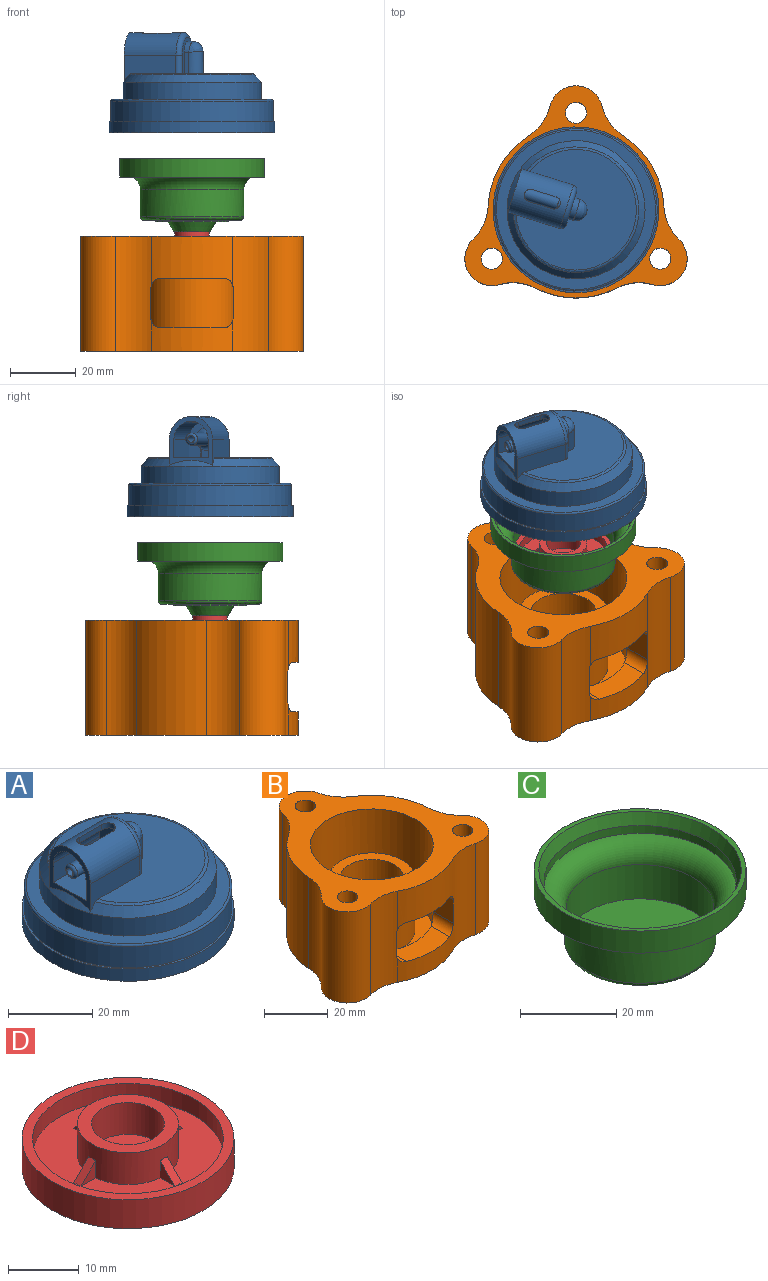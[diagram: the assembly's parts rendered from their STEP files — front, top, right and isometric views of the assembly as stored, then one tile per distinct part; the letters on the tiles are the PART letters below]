
ASSEMBLY  parts=4 mates=3
PART A: 80 faces, bbox 53.4x53.4x31 mm
  f0: plane 11x10.84mm, normal (-1,0,0), area 63mm2, adj f2,f65,f66,f67,f74,f75,f77
  f1: cylinder r=6.87mm len=16.5mm, axis (-1,0,0), area 315.8mm2, adj f9,f10,f55,f61,f70,f71,f72,f73
  f2: cylinder r=5.42mm len=15.2mm, axis (-1,0,0), area 218.2mm2, adj f0,f55,f65,f67,f70,f71,f72,f73
  f3: plane 2.2x2.2mm, normal (-1,0,0), area 0.7mm2, adj f62,f69
  f4: cone r=18.77mm half-angle=40deg, axis (0,0,-1), area 350.9mm2, adj f9,f10,f12,f27,f55
  f5: plane 6.43x1.45mm, normal (0,-1,0), area 9.3mm2, adj f6,f7,f11,f56
  f6: plane 11x10.74mm, normal (1,0,0), area 44.9mm2, adj f5,f8,f11,f56,f59,f60,f61
  f7: cylinder r=3.35mm len=6.8mm, axis (0,0,-1), area 70.2mm2, adj f5,f8,f11,f56,f57,f58
  f8: plane 6.45x1.45mm, normal (0,1,0), area 9.4mm2, adj f6,f7,f11,f56
  f9: plane 16.54x7.88mm, normal (0,-1,0), area 95.1mm2, adj f1,f4,f11,f12,f55,f60
  f10: plane 16.54x7.88mm, normal (0,1,0), area 95.1mm2, adj f1,f4,f11,f12,f55,f59
  f11: plane 36.6x35.27mm, normal (0,0,1), area 800.4mm2, adj f5,f6,f7,f8,f9,f10,f12,f59
  f12: torus R=18.3mm, axis (0,0,-1), area 90.3mm2, adj f4,f9,f10,f11
  f13: plane 36.6x36.6mm, normal (0,0,-1), area 1003.5mm2, adj f14,f29,f30,f31,f32,f35,f36,f37
  f14: cylinder r=18.3mm len=36.6mm, axis (0,0,-1), area 1494.8mm2, adj f13,f53
  f15: plane 38.5x38.5mm, normal (0,0,-1), area 6mm2, adj f53,f54
  f16: cylinder r=20.15mm len=40.3mm, axis (0,0,-1), area 312.7mm2, adj f17,f54
  f17: plane 43.8x43.8mm, normal (0,0,-1), area 231.2mm2, adj f16,f18
  f18: cylinder r=21.9mm len=43.8mm, axis (0,0,-1), area 371.5mm2, adj f17,f19
  f19: plane 47.3x47.3mm, normal (0,0,-1), area 250.4mm2, adj f18,f20
  f20: cylinder r=23.65mm len=47.3mm, axis (0,0,-1), area 662.7mm2, adj f19,f21
  f21: cone r=24.15mm half-angle=8deg, axis (0,0,-1), area 536.9mm2, adj f20,f22
  f22: plane 50.3x50.3mm, normal (0,0,-1), area 154.9mm2, adj f21,f23
  f23: cylinder r=25.15mm len=50.3mm, axis (0,0,-1), area 559.4mm2, adj f22,f24
  f24: plane 50.3x50.3mm, normal (0,0,1), area 78.2mm2, adj f23,f25
  f25: cylinder r=24.65mm len=49.3mm, axis (0,0,-1), area 944.8mm2, adj f24,f28
  f26: plane 48.3x48.3mm, normal (0,0,1), area 453.4mm2, adj f27,f28
  f27: cylinder r=20.95mm len=41.9mm, axis (0,0,-1), area 684.5mm2, adj f4,f26
  f28: torus R=24.15mm, axis (0,0,-1), area 120.7mm2, adj f25,f26
  f29: plane 2.8x1.4mm, normal (-1,0,0), area 3.9mm2, adj f13,f30,f32,f33
  f30: plane 6.66x2.8mm, normal (0,1,0), area 17.3mm2, adj f13,f29,f31,f33,f34
  f31: plane 1.4x0.3mm, normal (1,0,0), area 0.4mm2, adj f13,f30,f32,f34
  f32: plane 6.66x2.8mm, normal (0,-1,0), area 17.3mm2, adj f13,f29,f31,f33,f34
  f33: plane 4.16x1.4mm, normal (0,0,-1), area 5.8mm2, adj f29,f30,f32,f34
  f34: cylinder r=2.5mm len=2.5mm, axis (0,1,0), area 5.5mm2, adj f30,f31,f32,f33
  f35: plane 2.8x1.4mm, normal (0,-1,0), area 3.9mm2, adj f13,f36,f38,f39
  f36: plane 6.66x2.8mm, normal (-1,0,0), area 17.3mm2, adj f13,f35,f37,f39,f40
  f37: plane 1.4x0.3mm, normal (0,1,0), area 0.4mm2, adj f13,f36,f38,f40
  f38: plane 6.66x2.8mm, normal (1,0,0), area 17.3mm2, adj f13,f35,f37,f39,f40
  f39: plane 4.16x1.4mm, normal (0,0,-1), area 5.8mm2, adj f35,f36,f38,f40
  f40: cylinder r=2.5mm len=2.5mm, axis (-1,0,0), area 5.5mm2, adj f36,f37,f38,f39
  f41: plane 2.8x1.4mm, normal (1,0,0), area 3.9mm2, adj f13,f42,f44,f45
  f42: plane 6.66x2.8mm, normal (0,-1,0), area 17.3mm2, adj f13,f41,f43,f45,f46
  f43: plane 1.4x0.3mm, normal (-1,0,0), area 0.4mm2, adj f13,f42,f44,f46
  f44: plane 6.66x2.8mm, normal (0,1,0), area 17.3mm2, adj f13,f41,f43,f45,f46
  f45: plane 4.16x1.4mm, normal (0,0,-1), area 5.8mm2, adj f41,f42,f44,f46
  f46: cylinder r=2.5mm len=2.5mm, axis (0,-1,0), area 5.5mm2, adj f42,f43,f44,f45
  f47: plane 2.8x1.4mm, normal (0,1,0), area 3.9mm2, adj f13,f48,f50,f51
  f48: plane 6.66x2.8mm, normal (1,0,0), area 17.3mm2, adj f13,f47,f49,f51,f52
  f49: plane 1.4x0.3mm, normal (0,-1,0), area 0.4mm2, adj f13,f48,f50,f52
  f50: plane 6.66x2.8mm, normal (-1,0,0), area 17.3mm2, adj f13,f47,f49,f51,f52
  f51: plane 4.16x1.4mm, normal (0,0,-1), area 5.8mm2, adj f47,f48,f50,f52
  f52: cylinder r=2.5mm len=2.5mm, axis (1,0,0), area 5.5mm2, adj f48,f49,f50,f51
  f53: torus R=19.2mm, axis (0,0,1), area 165.5mm2, adj f14,f15
  f54: torus R=19.25mm, axis (0,0,1), area 176.1mm2, adj f15,f16
  f55: plane 14.73x13.75mm, normal (-1,0,0), area 62.5mm2, adj f1,f2,f4,f9,f10,f65,f66,f67
  f56: cylinder r=3.35mm len=6.7mm, axis (-1,0,0), area 17.6mm2, adj f5,f6,f7,f8,f57,f58
  f57: plane 0.02x0mm, normal (0,0,1), area 0mm2, adj f7,f56
  f58: bspline ~6.7x3.35mm, area 31.6mm2, adj f7,f56
  f59: cylinder r=1.5mm len=5.63mm, axis (0,0,-1), area 13.3mm2, adj f6,f10,f11,f61
  f60: cylinder r=1.5mm len=5.63mm, axis (0,0,1), area 13.3mm2, adj f6,f9,f11,f61
  f61: torus R=5.37mm, axis (1,0,0), area 46.8mm2, adj f1,f6,f59,f60
  f62: cylinder r=1mm len=17.83mm, axis (-1,0,0), area 112.1mm2, adj f3,f63
  f63: cylinder r=1.9mm len=9mm, axis (0,0,-1), area 104.2mm2, adj f13,f62,f64
  f64: plane 3.8x3.8mm, normal (0,0,-1), area 11.3mm2, adj f63
  f65: plane 15.2x5.58mm, normal (0,-1,0), area 84.8mm2, adj f0,f2,f55,f66
  f66: plane 16.4x10.84mm, normal (0,0,1), area 169mm2, adj f0,f55,f65,f67,f75,f77,f78
  f67: plane 15.2x5.58mm, normal (0,1,0), area 84.8mm2, adj f0,f2,f55,f66
  f68: cylinder r=1.85mm len=12.95mm, axis (-1,0,0), area 150.5mm2, adj f69,f74
  f69: torus R=1.1mm, axis (1,0,0), area 11.7mm2, adj f3,f68
  f70: cylinder r=1.9mm len=3.8mm, axis (0,0,-1), area 9.1mm2, adj f1,f2,f71,f73
  f71: plane 7.5x1.53mm, normal (0,1,0), area 11.4mm2, adj f1,f2,f70,f72
  f72: cylinder r=1.9mm len=3.8mm, axis (0,0,-1), area 9.1mm2, adj f1,f2,f71,f73
  f73: plane 7.5x1.53mm, normal (0,-1,0), area 11.4mm2, adj f1,f2,f70,f72
  f74: torus R=3.35mm, axis (-1,0,0), area 35.5mm2, adj f0,f68,f79
  f75: plane 3.73x1.2mm, normal (0,1,0), area 4.5mm2, adj f0,f66,f76,f78,f79
  f76: plane 3.5x1.2mm, normal (0,0,-1), area 4.2mm2, adj f75,f77,f78,f79
  f77: plane 3.73x1.2mm, normal (0,-1,0), area 4.5mm2, adj f0,f66,f76,f78,f79
  f78: plane 3.73x3.5mm, normal (-1,0,0), area 13.1mm2, adj f66,f75,f76,f77
  f79: plane 3.5x1.5mm, normal (1,0,0), area 4.7mm2, adj f74,f75,f76,f77
PART B: 31 faces, bbox 67.4x64.4x35 mm
  f0: cylinder r=26.68mm len=24.5mm, axis (0,0,1), area 328.9mm2, adj f1,f2,f15,f24,f27,f28
  f1: cylinder r=15mm len=35mm, axis (0,0,-1), area 394.7mm2, adj f0,f5,f6,f14,f15,f23,f27,f30
  f2: cylinder r=15mm len=35mm, axis (0,0,-1), area 394.7mm2, adj f0,f6,f7,f14,f15,f25,f28,f29
  f3: plane 38.55x38.55mm, normal (0,0,1), area 594.6mm2, adj f4,f21
  f4: cylinder r=19.28mm len=38.55mm, axis (0,0,1), area 3598.4mm2, adj f3,f15,f23,f24,f25,f26,f27,f28
  f5: cylinder r=8.17mm len=35mm, axis (0,0,1), area 759.4mm2, adj f1,f14,f15,f19
  f6: cylinder r=26.68mm len=24.5mm, axis (0,0,1), area 186.4mm2, adj f1,f2,f14,f26,f29,f30
  f7: cylinder r=8.17mm len=35mm, axis (0,0,1), area 759.4mm2, adj f2,f14,f15,f16
  f8: cylinder r=26.68mm len=35mm, axis (0,0,1), area 891mm2, adj f14,f15,f16,f17
  f9: cylinder r=8.17mm len=35mm, axis (0,0,1), area 759.4mm2, adj f14,f15,f17,f18
  f10: cylinder r=3.2mm len=35mm, axis (0,0,1), area 703.7mm2, adj f14,f15
  f11: cylinder r=3.2mm len=35mm, axis (0,0,1), area 703.7mm2, adj f14,f15
  f12: cylinder r=3.2mm len=35mm, axis (0,0,1), area 703.7mm2, adj f14,f15
  f13: cylinder r=26.68mm len=35mm, axis (0,0,1), area 891mm2, adj f14,f15,f18,f19
  f14: plane 67.45x64.35mm, normal (0,0,-1), area 2353.2mm2, adj f1,f2,f5,f6,f7,f8,f9,f10
  f15: plane 67.45x64.35mm, normal (0,0,1), area 1500.1mm2, adj f0,f1,f2,f4,f5,f7,f8,f9
  f16: cylinder r=15mm len=35mm, axis (0,0,-1), area 397.7mm2, adj f7,f8,f14,f15
  f17: cylinder r=15mm len=35mm, axis (0,0,-1), area 397.7mm2, adj f8,f9,f14,f15
  f18: cylinder r=15mm len=35mm, axis (0,0,-1), area 397.7mm2, adj f9,f13,f14,f15
  f19: cylinder r=15mm len=35mm, axis (0,0,-1), area 397.7mm2, adj f5,f13,f14,f15
  f20: cylinder r=10mm len=22.2mm, axis (0,0,-1), area 1394.9mm2, adj f14,f22
  f21: cylinder r=13.5mm len=27mm, axis (0,0,-1), area 1713.4mm2, adj f3,f22
  f22: plane 27x27mm, normal (0,0,1), area 258.4mm2, adj f20,f21
  f23: plane 9x8.9mm, normal (1,0,0), area 80.1mm2, adj f1,f4,f27,f30
  f24: plane 19x9.9mm, normal (0,0,-1), area 145.1mm2, adj f0,f4,f27,f28
  f25: plane 9x8.9mm, normal (-1,0,0), area 80.1mm2, adj f2,f4,f28,f29
  f26: plane 19x9.9mm, normal (0,0,1), area 145.1mm2, adj f4,f6,f29,f30
  f27: cylinder r=3mm len=10.25mm, axis (0,-1,0), area 40.5mm2, adj f0,f1,f4,f23,f24
  f28: cylinder r=3mm len=10.25mm, axis (0,1,0), area 40.5mm2, adj f0,f2,f4,f24,f25
  f29: cylinder r=3mm len=10.25mm, axis (0,-1,0), area 40.5mm2, adj f2,f4,f6,f25,f26
  f30: cylinder r=3mm len=10.25mm, axis (0,1,0), area 40.5mm2, adj f1,f4,f6,f23,f26
PART C: 18 faces, bbox 44x44x22.2 mm
  f0: cone r=20mm half-angle=19.3deg, axis (0,0,1), area 389mm2, adj f1,f16
  f1: cylinder r=20mm len=40mm, axis (0,0,1), area 251.3mm2, adj f0,f2
  f2: torus R=20mm, axis (0,0,1), area 782mm2, adj f1,f3
  f3: cylinder r=15.35mm len=30.7mm, axis (0,0,1), area 839.1mm2, adj f2,f4
  f4: plane 30.7x30.7mm, normal (0,0,1), area 700.6mm2, adj f3,f5
  f5: cylinder r=3.55mm len=7.1mm, axis (0,0,1), area 89.2mm2, adj f4,f6
  f6: plane 11x11mm, normal (0,0,-1), area 55.4mm2, adj f5,f7
  f7: cone r=7.35mm half-angle=30.8deg, axis (0,0,1), area 145.7mm2, adj f6,f8
  f8: plane 22.3x22.3mm, normal (0,0,-1), area 220.9mm2, adj f7,f9
  f9: cylinder r=11.15mm len=22.3mm, axis (0,0,1), area 28mm2, adj f8,f10
  f10: plane 29.4x29.4mm, normal (0,0,-1), area 288.3mm2, adj f9,f17
  f11: cylinder r=15.7mm len=31.4mm, axis (0,0,1), area 808.9mm2, adj f12,f17
  f12: torus R=20mm, axis (0,0,1), area 732.6mm2, adj f11,f13
  f13: cylinder r=20mm len=40mm, axis (0,0,1), area 50.3mm2, adj f12,f14
  f14: plane 44x44mm, normal (0,0,-1), area 263.9mm2, adj f13,f15
  f15: cylinder r=22mm len=44mm, axis (0,0,1), area 774.1mm2, adj f14,f16
  f16: plane 44x44mm, normal (0,0,1), area 135.1mm2, adj f0,f15
  f17: torus R=14.7mm, axis (0,0,-1), area 151.4mm2, adj f10,f11
PART D: 31 faces, bbox 30x30x13 mm
  f0: plane 27x27mm, normal (0,0,1), area 395.1mm2, adj f8,f9,f15,f16,f17,f19,f20,f21
  f1: plane 10.5x10.5mm, normal (0,0,-1), area 86.6mm2, adj f2
  f2: cylinder r=5.25mm len=10.5mm, axis (0,0,-1), area 44.5mm2, adj f1,f3
  f3: plane 10.5x10.5mm, normal (0,0,1), area 29.8mm2, adj f2,f4
  f4: cylinder r=4.25mm len=8.5mm, axis (0,0,-1), area 108.1mm2, adj f3,f5
  f5: plane 30x30mm, normal (0,0,-1), area 650.1mm2, adj f4,f6
  f6: cylinder r=15mm len=30mm, axis (0,0,-1), area 471.2mm2, adj f5,f7
  f7: plane 30x30mm, normal (0,0,1), area 134.3mm2, adj f6,f8
  f8: cylinder r=13.5mm len=27mm, axis (0,0,-1), area 246mm2, adj f0,f7
  f9: cylinder r=7.15mm len=14.3mm, axis (0,0,-1), area 230.3mm2, adj f0,f10,f15,f16,f18,f19,f20,f22
  f10: plane 14.3x14.3mm, normal (0,0,1), area 77.3mm2, adj f9,f11
  f11: cylinder r=5.15mm len=10.3mm, axis (0,0,-1), area 178mm2, adj f10,f12
  f12: plane 10.3x10.3mm, normal (0,0,1), area 74.2mm2, adj f11,f13
  f13: cylinder r=1.7mm len=3.4mm, axis (0,0,-1), area 17.1mm2, adj f12,f14
  f14: plane 3.4x3.4mm, normal (0,0,1), area 9.1mm2, adj f13
  f15: plane 3.03x3mm, normal (-1,0,0), area 4.6mm2, adj f0,f9,f17,f18
  f16: plane 3.03x3mm, normal (1,0,0), area 4.6mm2, adj f0,f9,f17,f18
  f17: plane 3x3mm, normal (0,-0.71,0.71), area 5.9mm2, adj f0,f15,f16,f18
  f18: plane 1.4x0.03mm, normal (0,0,1), area 0mm2, adj f9,f15,f16,f17
  f19: plane 3.03x3mm, normal (0,-1,0), area 4.6mm2, adj f0,f9,f21,f22
  f20: plane 3.03x3mm, normal (0,1,0), area 4.6mm2, adj f0,f9,f21,f22
  f21: plane 3x3mm, normal (0.71,0,0.71), area 5.9mm2, adj f0,f19,f20,f22
  f22: plane 1.4x0.03mm, normal (0,0,1), area 0mm2, adj f9,f19,f20,f21
  f23: plane 3.03x3mm, normal (1,0,0), area 4.6mm2, adj f0,f9,f25,f26
  f24: plane 3.03x3mm, normal (-1,0,0), area 4.6mm2, adj f0,f9,f25,f26
  f25: plane 3x3mm, normal (0,0.71,0.71), area 5.9mm2, adj f0,f23,f24,f26
  f26: plane 1.4x0.03mm, normal (0,0,1), area 0mm2, adj f9,f23,f24,f25
  f27: plane 3.03x3mm, normal (0,1,0), area 4.6mm2, adj f0,f9,f29,f30
  f28: plane 3.03x3mm, normal (0,-1,0), area 4.6mm2, adj f0,f9,f29,f30
  f29: plane 3x3mm, normal (-0.71,0,0.71), area 5.9mm2, adj f0,f27,f28,f30
  f30: plane 1.4x0.03mm, normal (0,0,1), area 0mm2, adj f9,f27,f28,f29
PLACE A rot(axis=(0,0,-1),17.4deg) t=(2.15,1.42,8.54)mm
PLACE B t=(2.15,1.42,-40.73)mm fixed
PLACE C rot(axis=(0,0,1),126.8deg) t=(2.15,1.42,-4.56)mm
PLACE D rot(axis=(0,0,1),126.8deg) t=(2.15,1.42,-4.56)mm
MATE cylindrical A.f4 <-> C.f0  axis (0,0,-1) through (2.15,1.42,-7.47)mm
MATE cylindrical B.f0 <-> C.f0  axis (0,0,1) through (2.15,1.42,-40.73)mm
MATE fastened D.f2 <-> C.f0  axis (0,0,1) through (2.15,1.42,-39.4)mm
